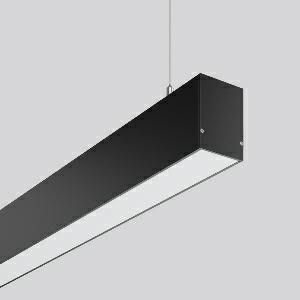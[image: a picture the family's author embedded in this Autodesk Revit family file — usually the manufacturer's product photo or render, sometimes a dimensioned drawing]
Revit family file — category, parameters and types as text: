
# Revit family: less_is_more_50_312312_003_150d
name_source: partatom
category: Lighting Fixtures
units: mm (PartAtom-declared; Revit-internal decimal feet)

## family parameters
Cut with Voids When Loaded = No
Host = Face
Light Source = No
Part Type = Normal
Room Calculation Point = No
Round Connector Dimension = Use Diameter
Shared = No

## types (1)
- LESS IS MORE 50 (1 x LED Modul 830, 3100 lm, 3000)
    Apparent Load = 28 VA
    CIE Flux Codes = 48 79 95 100 100
    Color Rendering = 80
    Color Temperature = 3000
    Default Elevation = 1800 mm
    Description = Series: LESS IS MORE 50
Linear pendant luminaire for aesthetically sophisticated lighting. Housing: extruded aluminium profile, powder-coated. End cap aluminium powder-coated. Canopy made of aluminium, powder-coated. Diffuser made of non-yellowing plastic (PMMA), opal. Direct light emission. Suitable for pendant. 2-point steel cable suspension freely positionable and infinitely height-adjustable. Special lengths available on request. LED unit with integrated converter interchangeable and removable. Suitable for through-wiring. With sensors or as a safety luminaire on request. 
Colour: deep black, matt (RAL 9005)
Length: 1127 mm
Width: 57 mm
Height: 75 mm
Suspension length: 2000 mm
Lamp: LED
Socket: without socket
Colour temperature: 3000K
Colour rendering index (CRI): 80
System power: 28 W
Rated luminous flux: 3100 lm
Luminous efficiency: 111 lm/W
Control gear: Regulated power supply
Protection class: I
Type of protection: IP 20
    Height = 75 mm
    Lamp = 1 x LED Modul 830
    Lamp Light Flux = 3100 lm
    Lamp count = 1
    Length = 1127 mm
    Lifetime = 50000 h
    Luminous efficacy = 111 lm/W
    Manufacturer = RZB
    ModVariant = No
    Model = 312312.003
    Mounting Place = Ceiling
    Mounting Type = Pendant
    Number of Poles = 1
    OnlyDefault = Yes
    Power Factor = 1
    Product Name = LESS IS MORE 50
    Product group = Pendant LED linear luminaires
    ProductGroupID = 907
    Protection Class = Protection class I
    Protection Degree = IP 20
    RLX_Detail_Level = 1
    RLX_Emergency_Light_Flux = 0 lm
    RLX_Emergency_Type = 0
    RLX_Emergency_Type_DB = No
    RlxData = <blob elided: 28861 chars, md5=65a98687>
    Socket = socket
    Standby Power = 0 W
    System Light Flux = 3100 lm
    System Power = 28 W
    Type Comments = Product without accessories
    Type Image = 312318.003.jpg
    URL = http://relux.com
    VarID = ---
    Voltage = 230 V
    Voltage Range = 220-240 V
    Weight = 0.00 kg
    Width = 57 mm

## geometry (parser evidence)
native form markers: Blend x4, Sweep x11
no freeform markers — native parametric forms only
